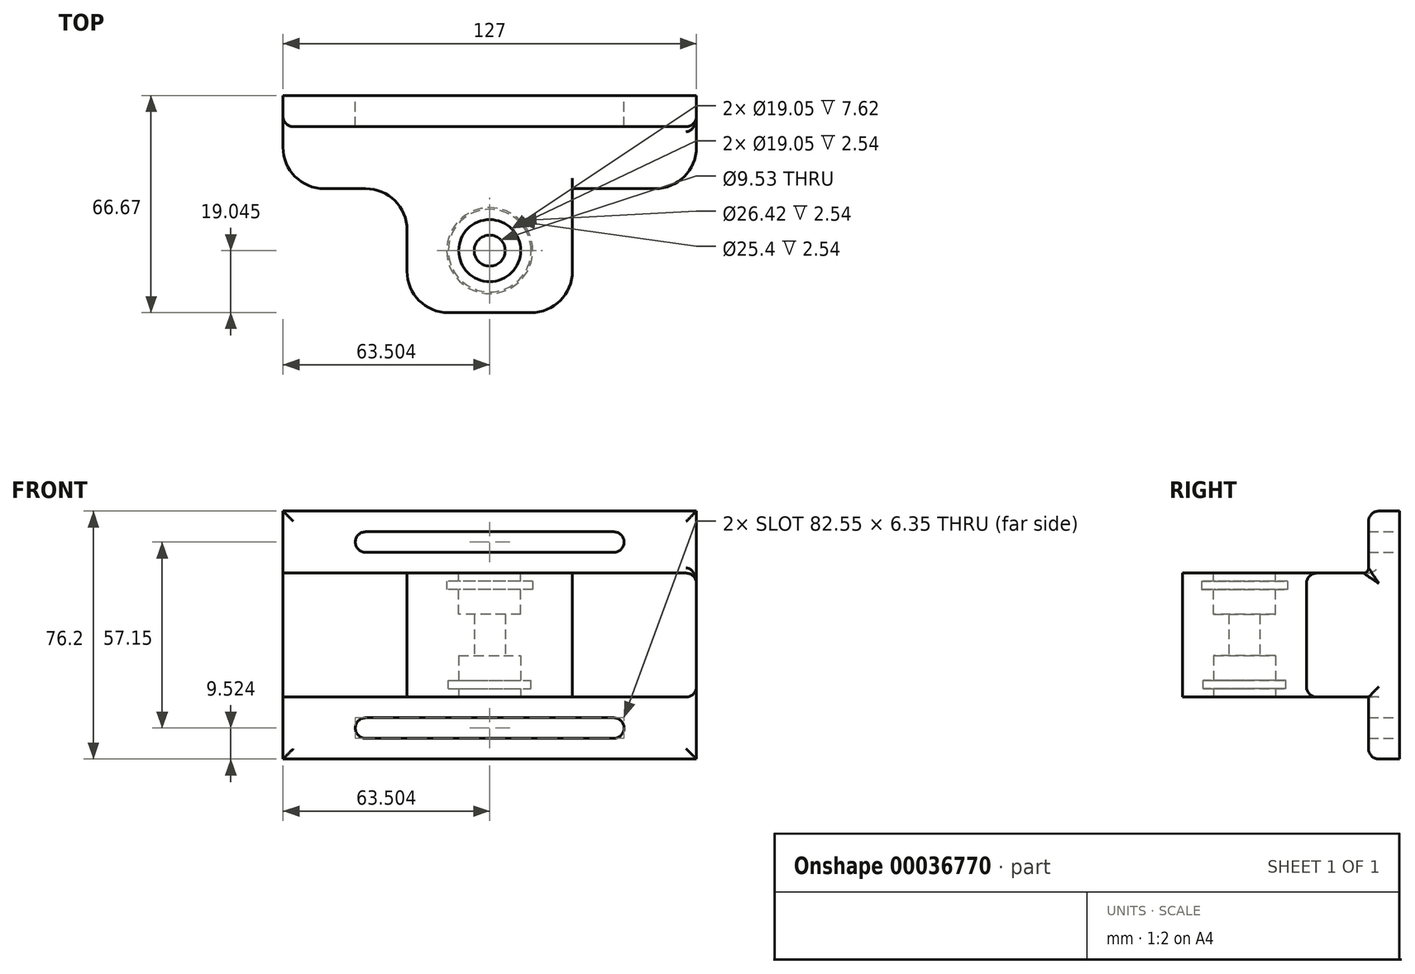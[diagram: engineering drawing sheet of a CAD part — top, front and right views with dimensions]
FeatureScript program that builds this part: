
annotation { "Feature Type Name" : "Feature", "Feature Type Description" : "" }
export const myFeature = defineFeature(function(context is Context, id is Id, definition is map)
    precondition{}
    {
        {
            var Q0;
            Q0=qCreatedBy(makeId("Front.planeOp"),FACE);
            var sketch = newSketch(context, id + "F0", { "sketchPlane" : qUnion([Q0])});
            skLineSegment(sketch, "E0.bottom", {"start": v(-66.45, -40.16) * mm, "end": v(60.55, -40.16) * mm});
            skLineSegment(sketch, "E0.top", {"start": v(-66.45, 36.04) * mm, "end": v(60.55, 36.04) * mm});
            skLineSegment(sketch, "E0.left", {"start": v(-66.45, -40.16) * mm, "end": v(-66.45, 36.04) * mm});
            skLineSegment(sketch, "E0.right", {"start": v(60.55, -40.16) * mm, "end": v(60.55, 36.04) * mm});
            skArc(sketch, "E1", {"start": v(-41.05, -27.46) * mm, "mid": v(-44.22, -30.64) * mm, "end": v(-41.05, -33.81) * mm});
            skArc(sketch, "E2", {"start": v(35.15, -33.81) * mm, "mid": v(38.33, -30.64) * mm, "end": v(35.15, -27.46) * mm});
            skLineSegment(sketch, "E3", {"start": v(-41.05, -27.46) * mm, "end": v(35.15, -27.46) * mm});
            skLineSegment(sketch, "E4", {"start": v(-41.05, -33.81) * mm, "end": v(35.15, -33.81) * mm});
            skLineSegment(sketch, "E5", {"start": v(-66.45, -2.06) * mm, "end": v(60.55, -2.06) * mm, "construction": true});
            skLineSegment(sketch, "E6.MirrorCS", {"start": v(-41.05, 23.34) * mm, "end": v(35.15, 23.34) * mm});
            skArc(sketch, "E7.MirrorCS", {"start": v(-41.05, 23.34) * mm, "mid": v(-44.22, 26.51) * mm, "end": v(-41.05, 29.69) * mm});
            skLineSegment(sketch, "E8.MirrorCS", {"start": v(-41.05, 29.69) * mm, "end": v(35.15, 29.69) * mm});
            skArc(sketch, "E9.MirrorCS", {"start": v(35.15, 29.69) * mm, "mid": v(38.33, 26.51) * mm, "end": v(35.15, 23.34) * mm});
            skSolve(sketch);
        }
        {
            var Q0;
            Q0=makeQuery(id+"F0.imprint","IMPRINT",FACE,{"disambiguationData":[TD([[makeQuery(id+"F0.imprint","IMPRINT",EDGE,{"derivedFrom":sQuery(id+"F0.wireOp",EDGE,"E0.bottom")}),1.0]])]});
            extrude(context, id + "F1", {"entities" : qUnion([Q0]), "depth" : 9.52 * mm});
        }
        {
            var Q0;
            Q0=makeQuery(id+"F1.opExtrude","CAP_FACE",FACE,{"disambiguationData":[OSD([sQuery(id+"F0.wireOp",EDGE,"E0.bottom"),sQuery(id+"F0.wireOp",EDGE,"E0.top"),sQuery(id+"F0.wireOp",EDGE,"E0.left"),sQuery(id+"F0.wireOp",EDGE,"E0.right"),sQuery(id+"F0.wireOp",EDGE,"E1"),sQuery(id+"F0.wireOp",EDGE,"E2"),sQuery(id+"F0.wireOp",EDGE,"E3"),sQuery(id+"F0.wireOp",EDGE,"E4"),sQuery(id+"F0.wireOp",EDGE,"E6.MirrorCS"),sQuery(id+"F0.wireOp",EDGE,"E7.MirrorCS"),sQuery(id+"F0.wireOp",EDGE,"E8.MirrorCS"),sQuery(id+"F0.wireOp",EDGE,"E9.MirrorCS")])],"isStart":false});
            var sketch = newSketch(context, id + "F2", { "sketchPlane" : qUnion([Q0])});
            skLineSegment(sketch, "E10.bottom", {"start": v(-66.45, -21.11) * mm, "end": v(60.55, -21.11) * mm});
            skLineSegment(sketch, "E10.top", {"start": v(-66.45, 16.99) * mm, "end": v(60.55, 16.99) * mm});
            skLineSegment(sketch, "E10.left", {"start": v(-66.45, -21.11) * mm, "end": v(-66.45, 16.99) * mm});
            skLineSegment(sketch, "E10.right", {"start": v(60.55, -21.11) * mm, "end": v(60.55, 16.99) * mm});
            skSolve(sketch);
        }
        {
            var Q0;
            Q0=makeQuery(id+"F2.imprint","IMPRINT",FACE,{"disambiguationData":[TD([[makeQuery(id+"F2.imprint","IMPRINT",EDGE,{"derivedFrom":sQuery(id+"F2.wireOp",EDGE,"E10.bottom")}),1.0]])]});
            extrude(context, id + "F3", {"entities" : qUnion([Q0]), "operationType" : NewBodyOperationType.ADD, "depth" : 19.05 * mm});
        }
        {
            var Q0;
            Q0=makeQuery(id+"F3.opExtrude","CAP_FACE",FACE,{"disambiguationData":[OSD([sQuery(id+"F2.wireOp",EDGE,"E10.bottom"),sQuery(id+"F2.wireOp",EDGE,"E10.top"),sQuery(id+"F2.wireOp",EDGE,"E10.left"),sQuery(id+"F2.wireOp",EDGE,"E10.right")])],"isStart":false});
            var sketch = newSketch(context, id + "F4", { "sketchPlane" : qUnion([Q0])});
            skLineSegment(sketch, "E11.bottom", {"start": v(-28.35, -21.11) * mm, "end": v(22.45, -21.11) * mm});
            skLineSegment(sketch, "E11.top", {"start": v(-28.35, 16.99) * mm, "end": v(22.45, 16.99) * mm});
            skLineSegment(sketch, "E11.left", {"start": v(-28.35, -21.11) * mm, "end": v(-28.35, 16.99) * mm});
            skLineSegment(sketch, "E11.right", {"start": v(22.45, -21.11) * mm, "end": v(22.45, 16.99) * mm});
            skSolve(sketch);
        }
        {
            var Q0;
            Q0=makeQuery(id+"F4.imprint","IMPRINT",FACE,{"disambiguationData":[TD([[makeQuery(id+"F4.imprint","IMPRINT",EDGE,{"derivedFrom":sQuery(id+"F4.wireOp",EDGE,"E11.bottom")}),1.0]])]});
            extrude(context, id + "F5", {"entities" : qUnion([Q0]), "operationType" : NewBodyOperationType.ADD, "depth" : 38.1 * mm});
        }
        {
            var Q0;
            Q0=makeQuery(id+"F5.boolean.opBoolean","MERGE",FACE,{"derivedFrom":[makeQuery(id+"F3.opExtrude","SWEPT_FACE",FACE,{"disambiguationData":[OSD([sQuery(id+"F2.wireOp",EDGE,"E10.bottom")])]}),makeQuery(id+"F5.opExtrude","SWEPT_FACE",FACE,{"disambiguationData":[OSD([sQuery(id+"F4.wireOp",EDGE,"E11.bottom")])]})]});
            var sketch = newSketch(context, id + "F6", { "sketchPlane" : qUnion([Q0])});
            skPoint(sketch, "E12", {"position": v(-2.95, 47.63) * mm});
            skSolve(sketch);
        }
        {
            var Q0;
            Q0=sQuery(id+"F6.wireOp",VERTEX,"E12");
            var Q1;
            Q1=makeQuery(id+"F1.opExtrude","SWEPT_BODY",BODY,{"disambiguationData":[OSD([sQuery(id+"F0.wireOp",EDGE,"E0.bottom"),sQuery(id+"F0.wireOp",EDGE,"E0.top"),sQuery(id+"F0.wireOp",EDGE,"E0.left"),sQuery(id+"F0.wireOp",EDGE,"E0.right"),sQuery(id+"F0.wireOp",EDGE,"E1"),sQuery(id+"F0.wireOp",EDGE,"E2"),sQuery(id+"F0.wireOp",EDGE,"E3"),sQuery(id+"F0.wireOp",EDGE,"E4"),sQuery(id+"F0.wireOp",EDGE,"E6.MirrorCS"),sQuery(id+"F0.wireOp",EDGE,"E7.MirrorCS"),sQuery(id+"F0.wireOp",EDGE,"E8.MirrorCS"),sQuery(id+"F0.wireOp",EDGE,"E9.MirrorCS")])]});
            hole(context, id + "F7", {"style" : HoleStyle.SIMPLE, "holeDiameter" : 9.52 * mm, "endStyle" : HoleEndStyle.THROUGH, "locations" : qUnion([Q0]), "scope" : qUnion([Q1])});
        }
        {
            var Q0;
            Q0=makeQuery(id+"F5.boolean.opBoolean","MERGE",FACE,{"derivedFrom":[makeQuery(id+"F3.opExtrude","SWEPT_FACE",FACE,{"disambiguationData":[OSD([sQuery(id+"F2.wireOp",EDGE,"E10.bottom")])]}),makeQuery(id+"F5.opExtrude","SWEPT_FACE",FACE,{"disambiguationData":[OSD([sQuery(id+"F4.wireOp",EDGE,"E11.bottom")])]})]});
            var sketch = newSketch(context, id + "F8", { "sketchPlane" : qUnion([Q0])});
            skCircle(sketch, "E13", {"center": v(-2.95, 47.63) * mm, "radius": 9.53 * mm});
            skSolve(sketch);
        }
        {
            var Q0;
            Q0=makeQuery(id+"F8.imprint","IMPRINT",FACE,{"disambiguationData":[TD([[makeQuery(id+"F8.imprint","IMPRINT",EDGE,{"derivedFrom":sQuery(id+"F8.wireOp",EDGE,"E13")}),1.0]])]});
            extrude(context, id + "F9", {"entities" : qUnion([Q0]), "operationType" : NewBodyOperationType.REMOVE, "oppositeDirection" : true, "depth" : 12.7 * mm});
        }
        {
            var Q0;
            Q0=makeQuery(id+"F5.boolean.opBoolean","MERGE",FACE,{"derivedFrom":[makeQuery(id+"F3.opExtrude","SWEPT_FACE",FACE,{"disambiguationData":[OSD([sQuery(id+"F2.wireOp",EDGE,"E10.top")])]}),makeQuery(id+"F5.opExtrude","SWEPT_FACE",FACE,{"disambiguationData":[OSD([sQuery(id+"F4.wireOp",EDGE,"E11.top")])]})]});
            var sketch = newSketch(context, id + "F10", { "sketchPlane" : qUnion([Q0])});
            skLineSegment(sketch, "E14.0.0", {"start": v(60.55, -9.53) * mm, "end": v(-66.45, -9.53) * mm});
            skLineSegment(sketch, "E14.0.1", {"start": v(-66.45, -9.53) * mm, "end": v(-66.45, -28.58) * mm});
            skLineSegment(sketch, "E14.0.2", {"start": v(-66.45, -28.58) * mm, "end": v(-28.35, -28.58) * mm});
            skLineSegment(sketch, "E14.0.3", {"start": v(-28.35, -28.58) * mm, "end": v(-28.35, -66.68) * mm});
            skLineSegment(sketch, "E14.0.4", {"start": v(-28.35, -66.68) * mm, "end": v(22.45, -66.68) * mm});
            skLineSegment(sketch, "E14.0.5", {"start": v(22.45, -66.68) * mm, "end": v(22.45, -28.58) * mm});
            skLineSegment(sketch, "E14.0.6", {"start": v(22.45, -28.58) * mm, "end": v(60.55, -28.58) * mm});
            skLineSegment(sketch, "E14.0.7", {"start": v(60.55, -28.58) * mm, "end": v(60.55, -9.53) * mm});
            skCircle(sketch, "E15.0", {"center": v(-2.95, -47.63) * mm, "radius": 9.53 * mm});
            skSolve(sketch);
        }
        {
            var Q0;
            Q0=makeQuery(id+"F10.imprint","IMPRINT",FACE,{"disambiguationData":[TD([[makeQuery(id+"F10.imprint","IMPRINT",EDGE,{"derivedFrom":sQuery(id+"F10.wireOp",EDGE,"E15.0")}),1.0]])]});
            extrude(context, id + "F11", {"entities" : qUnion([Q0]), "operationType" : NewBodyOperationType.REMOVE, "oppositeDirection" : true, "depth" : 12.7 * mm});
        }
        {
            var Q0;
            Q0=makeQuery(id+"F1.opExtrude","SWEPT_FACE",FACE,{"disambiguationData":[OSD([sQuery(id+"F0.wireOp",EDGE,"E0.top")])]});
            cPlane(context, id + "F12", {"entities" : qUnion([Q0]), "cplaneType" : CPlaneType.OFFSET, "offset" : 24.13 * mm, "oppositeDirection" : true, "width" : 152.4 * mm, "height" : 152.4 * mm});
        }
        {
            var Q0;
            Q0=qCreatedBy(id+"F12.planeOp",FACE);
            var sketch = newSketch(context, id + "F13", { "sketchPlane" : qUnion([Q0])});
            skCircle(sketch, "E16", {"center": v(-2.95, -47.63) * mm, "radius": 13.21 * mm});
            skSolve(sketch);
        }
        {
            var Q0;
            Q0 = qSketchRegion(id + "F13", true);
            var Q1;
            Q1=makeQuery(id+"F5.boolean.opBoolean","MERGE",FACE,{"derivedFrom":[makeQuery(id+"F3.opExtrude","SWEPT_FACE",FACE,{"disambiguationData":[OSD([sQuery(id+"F2.wireOp",EDGE,"E10.top")])]}),makeQuery(id+"F5.opExtrude","SWEPT_FACE",FACE,{"disambiguationData":[OSD([sQuery(id+"F4.wireOp",EDGE,"E11.top")])]})]});
            extrude(context, id + "F14", {"entities" : qUnion([Q0, Q1]), "operationType" : NewBodyOperationType.REMOVE, "depth" : 2.54 * mm});
        }
        {
            var Q0;
            Q0=makeQuery(id+"F1.opExtrude","SWEPT_FACE",FACE,{"disambiguationData":[OSD([sQuery(id+"F0.wireOp",EDGE,"E0.bottom")])]});
            cPlane(context, id + "F15", {"entities" : qUnion([Q0]), "cplaneType" : CPlaneType.OFFSET, "offset" : 24.13 * mm, "oppositeDirection" : true, "width" : 152.4 * mm, "height" : 152.4 * mm});
        }
        {
            var Q0;
            Q0=qCreatedBy(id+"F15.planeOp",FACE);
            var sketch = newSketch(context, id + "F16", { "sketchPlane" : qUnion([Q0])});
            skCircle(sketch, "E17", {"center": v(-2.95, 47.63) * mm, "radius": 12.7 * mm});
            skSolve(sketch);
        }
        {
            var Q0;
            Q0 = qSketchRegion(id + "F16", true);
            var Q1;
            Q1=makeQuery(id+"F5.boolean.opBoolean","MERGE",FACE,{"derivedFrom":[makeQuery(id+"F3.opExtrude","SWEPT_FACE",FACE,{"disambiguationData":[OSD([sQuery(id+"F2.wireOp",EDGE,"E10.bottom")])]}),makeQuery(id+"F5.opExtrude","SWEPT_FACE",FACE,{"disambiguationData":[OSD([sQuery(id+"F4.wireOp",EDGE,"E11.bottom")])]})]});
            extrude(context, id + "F17", {"entities" : qUnion([Q0, Q1]), "operationType" : NewBodyOperationType.REMOVE, "depth" : 2.54 * mm});
        }
        {
            var Q0;
            Q0=makeQuery(id+"F5.opExtrude","CAP_EDGE",EDGE,{"disambiguationData":[OSD([sQuery(id+"F4.wireOp",EDGE,"E11.right")])],"isStart":false});
            var Q1;
            Q1=makeQuery(id+"F5.opExtrude","CAP_EDGE",EDGE,{"disambiguationData":[OSD([sQuery(id+"F4.wireOp",EDGE,"E11.right")])],"isStart":true});
            var Q2;
            Q2=makeQuery(id+"F3.opExtrude","CAP_EDGE",EDGE,{"disambiguationData":[OSD([sQuery(id+"F2.wireOp",EDGE,"E10.right")])],"isStart":false});
            var Q3;
            Q3=makeQuery(id+"F5.opExtrude","CAP_EDGE",EDGE,{"disambiguationData":[OSD([sQuery(id+"F4.wireOp",EDGE,"E11.left")])],"isStart":false});
            var Q4;
            Q4=makeQuery(id+"F5.opExtrude","CAP_EDGE",EDGE,{"disambiguationData":[OSD([sQuery(id+"F4.wireOp",EDGE,"E11.left")])],"isStart":true});
            var Q5;
            Q5=makeQuery(id+"F3.opExtrude","CAP_EDGE",EDGE,{"disambiguationData":[OSD([sQuery(id+"F2.wireOp",EDGE,"E10.left")])],"isStart":false});
            fillet(context, id + "F18", {"entities" : qUnion([Q0, Q1, Q2, Q3, Q4, Q5]), "radius" : 12.7 * mm, "tangentPropagation" : true, "allowEdgeOverflow" : false});
        }
        {
            var Q0;
            Q0=makeQuery(id+"F1.opExtrude","CAP_EDGE",EDGE,{"disambiguationData":[OSD([sQuery(id+"F0.wireOp",EDGE,"E0.bottom")])],"isStart":false});
            var Q1;
            Q1=makeQuery(id+"F3.opExtrude","SWEPT_EDGE",EDGE,{"disambiguationData":[OSD([sQuery(id+"F0.wireOp",EDGE,"E0.right"),sQuery(id+"F2.wireOp",EDGE,"E10.bottom"),sQuery(id+"F2.wireOp",EDGE,"E10.right")])]});
            var Q2;
            Q2=makeQuery(id+"F18.opFillet","BLEND_EDGE",EDGE,{"blendedFrom":[makeQuery(id+"F3.opExtrude","CAP_EDGE",EDGE,{"disambiguationData":[OSD([sQuery(id+"F2.wireOp",EDGE,"E10.right")])],"isStart":false}),makeQuery(id+"F5.boolean.opBoolean","MERGE",FACE,{"derivedFrom":[makeQuery(id+"F3.opExtrude","SWEPT_FACE",FACE,{"disambiguationData":[OSD([sQuery(id+"F2.wireOp",EDGE,"E10.bottom")])]}),makeQuery(id+"F5.opExtrude","SWEPT_FACE",FACE,{"disambiguationData":[OSD([sQuery(id+"F4.wireOp",EDGE,"E11.bottom")])]})]})],"blendedInto":[makeQuery(id+"F5.boolean.opBoolean","MERGE",FACE,{"derivedFrom":[makeQuery(id+"F3.opExtrude","SWEPT_FACE",FACE,{"disambiguationData":[OSD([sQuery(id+"F2.wireOp",EDGE,"E10.bottom")])]}),makeQuery(id+"F5.opExtrude","SWEPT_FACE",FACE,{"disambiguationData":[OSD([sQuery(id+"F4.wireOp",EDGE,"E11.bottom")])]})]})]});
            var Q3;
            Q3=makeQuery(id+"F18.opFillet","BLEND_EDGE",EDGE,{"blendedFrom":[makeQuery(id+"F5.opExtrude","CAP_EDGE",EDGE,{"disambiguationData":[OSD([sQuery(id+"F4.wireOp",EDGE,"E11.right")])],"isStart":true}),makeQuery(id+"F5.boolean.opBoolean","MERGE",FACE,{"derivedFrom":[makeQuery(id+"F3.opExtrude","SWEPT_FACE",FACE,{"disambiguationData":[OSD([sQuery(id+"F2.wireOp",EDGE,"E10.bottom")])]}),makeQuery(id+"F5.opExtrude","SWEPT_FACE",FACE,{"disambiguationData":[OSD([sQuery(id+"F4.wireOp",EDGE,"E11.bottom")])]})]})],"blendedInto":[makeQuery(id+"F5.boolean.opBoolean","MERGE",FACE,{"derivedFrom":[makeQuery(id+"F3.opExtrude","SWEPT_FACE",FACE,{"disambiguationData":[OSD([sQuery(id+"F2.wireOp",EDGE,"E10.bottom")])]}),makeQuery(id+"F5.opExtrude","SWEPT_FACE",FACE,{"disambiguationData":[OSD([sQuery(id+"F4.wireOp",EDGE,"E11.bottom")])]})]})]});
            var Q4;
            {var subQ0=sQuery(id+"F2.wireOp",EDGE,"E10.bottom");Q4=makeQuery(id+"F5.boolean.opBoolean","SPLIT",EDGE,{"disambiguationData":[TD([makeQuery(id+"F1.opExtrude","SWEPT_FACE",FACE,{"disambiguationData":[OSD([sQuery(id+"F0.wireOp",EDGE,"E0.right")])]})])],"derivedFrom":makeQuery(id+"F3.opExtrude","CAP_EDGE",EDGE,{"disambiguationData":[OSD([subQ0])],"isStart":false})});}
            var Q5;
            Q5=makeQuery(id+"F18.opFillet","BLEND_EDGE",EDGE,{"blendedFrom":[makeQuery(id+"F3.opExtrude","CAP_EDGE",EDGE,{"disambiguationData":[OSD([sQuery(id+"F2.wireOp",EDGE,"E10.right")])],"isStart":false}),makeQuery(id+"F5.boolean.opBoolean","MERGE",FACE,{"derivedFrom":[makeQuery(id+"F3.opExtrude","SWEPT_FACE",FACE,{"disambiguationData":[OSD([sQuery(id+"F2.wireOp",EDGE,"E10.top")])]}),makeQuery(id+"F5.opExtrude","SWEPT_FACE",FACE,{"disambiguationData":[OSD([sQuery(id+"F4.wireOp",EDGE,"E11.top")])]})]})],"blendedInto":[makeQuery(id+"F5.boolean.opBoolean","MERGE",FACE,{"derivedFrom":[makeQuery(id+"F3.opExtrude","SWEPT_FACE",FACE,{"disambiguationData":[OSD([sQuery(id+"F2.wireOp",EDGE,"E10.top")])]}),makeQuery(id+"F5.opExtrude","SWEPT_FACE",FACE,{"disambiguationData":[OSD([sQuery(id+"F4.wireOp",EDGE,"E11.top")])]})]})]});
            var Q6;
            Q6=makeQuery(id+"F3.opExtrude","SWEPT_EDGE",EDGE,{"disambiguationData":[OSD([sQuery(id+"F0.wireOp",EDGE,"E0.right"),sQuery(id+"F2.wireOp",EDGE,"E10.top"),sQuery(id+"F2.wireOp",EDGE,"E10.right")])]});
            var Q7;
            Q7=makeQuery(id+"F1.opExtrude","CAP_EDGE",EDGE,{"disambiguationData":[OSD([sQuery(id+"F0.wireOp",EDGE,"E0.top")])],"isStart":false});
            var Q8;
            {var subQ0=sQuery(id+"F0.wireOp",EDGE,"E0.right");var subQ1=sQuery(id+"F0.wireOp",EDGE,"E0.top");Q8=makeQuery(id+"F3.boolean.opBoolean","SPLIT",EDGE,{"disambiguationData":[TD([makeQuery(id+"F1.opExtrude","SWEPT_FACE",FACE,{"disambiguationData":[OSD([subQ1])]})])],"derivedFrom":makeQuery(id+"F1.opExtrude","CAP_EDGE",EDGE,{"disambiguationData":[OSD([subQ0])],"isStart":false})});}
            var Q9;
            {var subQ0=sQuery(id+"F0.wireOp",EDGE,"E0.right");var subQ1=sQuery(id+"F0.wireOp",EDGE,"E0.bottom");Q9=makeQuery(id+"F3.boolean.opBoolean","SPLIT",EDGE,{"disambiguationData":[TD([makeQuery(id+"F1.opExtrude","SWEPT_FACE",FACE,{"disambiguationData":[OSD([subQ1])]})])],"derivedFrom":makeQuery(id+"F1.opExtrude","CAP_EDGE",EDGE,{"disambiguationData":[OSD([subQ0])],"isStart":false})});}
            var Q10;
            {var subQ0=sQuery(id+"F0.wireOp",EDGE,"E0.left");var subQ1=sQuery(id+"F0.wireOp",EDGE,"E0.top");Q10=makeQuery(id+"F3.boolean.opBoolean","SPLIT",EDGE,{"disambiguationData":[TD([makeQuery(id+"F1.opExtrude","SWEPT_FACE",FACE,{"disambiguationData":[OSD([subQ1])]})])],"derivedFrom":makeQuery(id+"F1.opExtrude","CAP_EDGE",EDGE,{"disambiguationData":[OSD([subQ0])],"isStart":false})});}
            var Q11;
            {var subQ0=sQuery(id+"F0.wireOp",EDGE,"E0.left");var subQ1=sQuery(id+"F0.wireOp",EDGE,"E0.bottom");Q11=makeQuery(id+"F3.boolean.opBoolean","SPLIT",EDGE,{"disambiguationData":[TD([makeQuery(id+"F1.opExtrude","SWEPT_FACE",FACE,{"disambiguationData":[OSD([subQ1])]})])],"derivedFrom":makeQuery(id+"F1.opExtrude","CAP_EDGE",EDGE,{"disambiguationData":[OSD([subQ0])],"isStart":false})});}
            fillet(context, id + "F19", {"entities" : qUnion([Q0, Q1, Q2, Q3, Q4, Q5, Q6, Q7, Q8, Q9, Q10, Q11]), "radius" : 3.17 * mm, "tangentPropagation" : true, "allowEdgeOverflow" : false});
        }
        {
            var Q0;
            Q0=makeQuery(id+"F3.opExtrude","CAP_EDGE",EDGE,{"disambiguationData":[OSD([sQuery(id+"F2.wireOp",EDGE,"E10.bottom")])],"isStart":true});
            var Q1;
            Q1=makeQuery(id+"F3.opExtrude","CAP_EDGE",EDGE,{"disambiguationData":[OSD([sQuery(id+"F2.wireOp",EDGE,"E10.top")])],"isStart":true});
            fillet(context, id + "F20", {"entities" : qUnion([Q0, Q1]), "radius" : 1.59 * mm, "tangentPropagation" : true, "allowEdgeOverflow" : false});
        }
    });
